# Revit family: Diverter-3_Way-Two_Handle-Grohe-Timeless-29427_Series
name_source: partatom
category: Plumbing Fixtures
units: mm (PartAtom-declared; Revit-internal decimal feet)

## family parameters
Cut with Voids When Loaded = No
Host = Face
OmniClass Number = 23.65.55.14
OmniClass Title = Valves for Liquid Services
Part Type = Normal
Room Calculation Point = No
Round Connector Dimension = Use Diameter
Shared = Yes

## types (5) — shared parameters
ADA Compliant = Yes
ASME A112.18.1/CSA B125.1/ASSE 1016 = Yes
Assembly Code = D2020300
CEC Compliant = Yes
CW Connection = Yes
CWFU = 3
Cold Water Connection Diameter = 1/2"
Compliance Certifications = CALGreen Compliant, Massachusetts Plumbing Board Approved,
Default Elevation = 48"
Description = TIMELESS- Pressure Balance Valve Trim With 3-Way Diverter With Cartridge
Diameter = 7 7/8"
HW Connection = Yes
HWFU = 3
Height = 9 1/4"
Hot Water Connection Diameter = 1"
Installation Type = Wall Mounted
Length = 2 3/4"
Manufacturer = GROHE
Price = Prices may vary. Please consult Manufacturer Representative for most up-to-date price list.
Tempered Water Connection = Yes
Tempered Water Connection Diameter = 1/2"
URL = https://www.grohe.us
Vent Connection = No
WFU = 4
Waste Connection = No

## per-type parameters (varying)
| type | Finish | Material |
| 29427000 | Metal-Grohe-000-StarLight Chrome | Metal-Grohe-000-StarLight Chrome |
| 294272430 | Metal-Grohe-430-Matte Black | Metal-Grohe-430-Matte Black |
| 29427A00 | Metal-Grohe-A00-Hard Graphite | Metal-Grohe-A00-Hard Graphite |
| 29427EN0 | Metal-Grohe-EN0-Brushed Nickel Infinity Finish | Metal-Grohe-EN0-Brushed Nickel Infinity Finish |
| 29427GN0 | Metal-Grohe-GN0-Brushed Cool Sunrise | Metal-Grohe-GN0-Brushed Cool Sunrise |

note: column(s) folded — value = type name in every type: Model

## geometry (parser evidence)
native form markers: Sweep x3
no freeform markers — native parametric forms only
